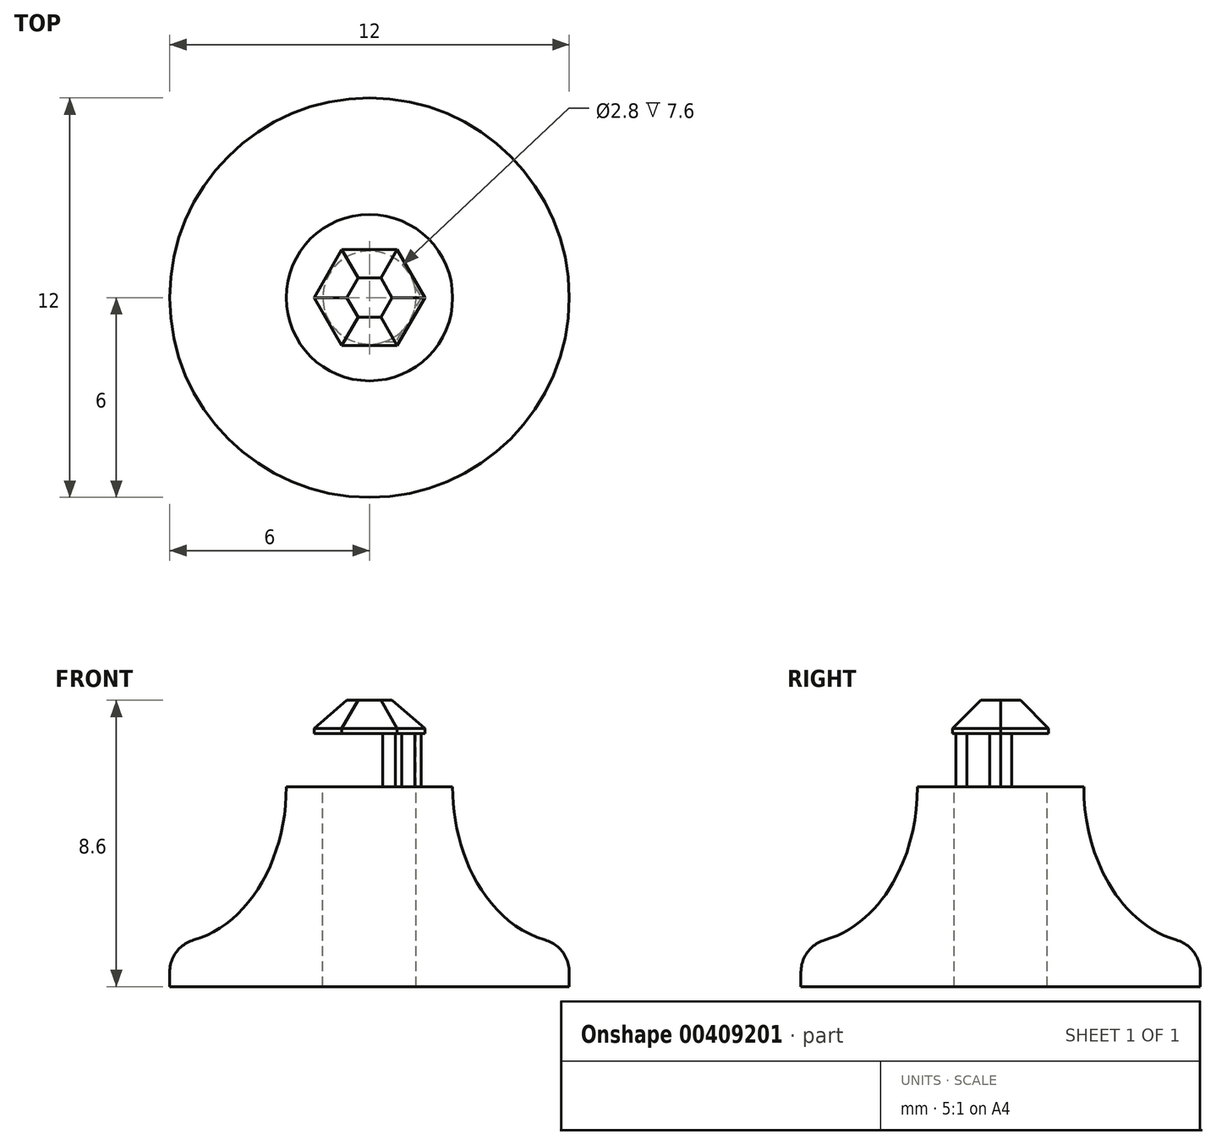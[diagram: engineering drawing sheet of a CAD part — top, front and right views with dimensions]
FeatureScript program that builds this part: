
annotation { "Feature Type Name" : "Feature", "Feature Type Description" : "" }
export const myFeature = defineFeature(function(context is Context, id is Id, definition is map)
    precondition{}
    {
        {
            var Q0;
            Q0=qCreatedBy(makeId("Front.planeOp"),FACE);
            var sketch = newSketch(context, id + "F0", { "sketchPlane" : qUnion([Q0])});
            skLineSegment(sketch, "E0.bottom", {"start": v(0, 0) * mm, "end": v(6, 0) * mm});
            skLineSegment(sketch, "E0.top", {"start": v(0, 6) * mm, "end": v(2.5, 6) * mm});
            skLineSegment(sketch, "E0.left", {"start": v(0, 0) * mm, "end": v(0, 6) * mm});
            skLineSegment(sketch, "E0.right", {"start": v(6, 0) * mm, "end": v(6, 0.44) * mm});
            skEllipticalArc(sketch, "E1", {});
            skPoint(sketch, "E2", {"position": v(2.5, 6) * mm});
            skPoint(sketch, "E3", {"position": v(6, 1.3) * mm});
            skPoint(sketch, "E4.visualSharp", {"position": v(0, 6) * mm});
            skArc(sketch, "E5.filletArc", {"start": v(6, 0.44) * mm, "mid": v(5.8, 1.04) * mm, "end": v(5.27, 1.4) * mm});
            const initialGuessF0  = {"E1": [0.006, 0.006, -1, 0, 0.0035, 0.0047, 6.283185307179586, 1.3618196011728392]};
            skSetInitialGuess(sketch, initialGuessF0);
            skSolve(sketch);
        }
        {
            var Q0;
            Q0=makeQuery(id+"F0.imprint","IMPRINT",FACE,{"disambiguationData":[TD([[makeQuery(id+"F0.imprint","IMPRINT",EDGE,{"derivedFrom":sQuery(id+"F0.wireOp",EDGE,"E0.bottom")}),1.0]])]});
            var Q1;
            Q1=sQuery(id+"F0.wireOp",EDGE,"E0.left");
            revolve(context, id + "F1", {"entities" : qUnion([Q0]), "axis" : qUnion([Q1]), "revolveType" : RevolveType.FULL});
        }
        {
            var Q0;
            Q0=makeQuery(id+"F1.opRevolve","SWEPT_BODY",BODY,{"disambiguationData":[OSD([sQuery(id+"F0.wireOp",EDGE,"E0.bottom"),sQuery(id+"F0.wireOp",EDGE,"E0.top"),sQuery(id+"F0.wireOp",EDGE,"E0.left"),sQuery(id+"F0.wireOp",EDGE,"E0.right"),sQuery(id+"F0.wireOp",EDGE,"E1"),sQuery(id+"F0.wireOp",EDGE,"ArTpo5st-Iq33-hNdW-1lph-2rlKh8i0XKDo"),sQuery(id+"F0.wireOp",EDGE,"E5.filletArc")])]});
            transform(context, id + "F2", {"entities" : qUnion([Q0]), "transformType" : TransformType.TRANSLATION_3D, "dx" : 0 * mm, "dy" : 0 * mm, "dz" : 0 * mm, "makeCopy" : true});
        }
        {
            var Q0;
            Q0=makeQuery(id+"F1.opRevolve","SWEPT_FACE",FACE,{"disambiguationData":[OSD([sQuery(id+"F0.wireOp",EDGE,"E0.top")])]});
            var sketch = newSketch(context, id + "F3", { "sketchPlane" : qUnion([Q0])});
            skCircle(sketch, "E6", {"center": v(0, 0) * mm, "radius": 1.4 * mm});
            skSolve(sketch);
        }
        {
            var Q0;
            Q0=makeQuery(id+"F3.imprint","IMPRINT",FACE,{"disambiguationData":[TD([[makeQuery(id+"F3.imprint","IMPRINT",EDGE,{"derivedFrom":sQuery(id+"F3.wireOp",EDGE,"E6")}),1.0]])]});
            extrude(context, id + "F4", {"entities" : qUnion([Q0]), "operationType" : NewBodyOperationType.REMOVE, "endBound" : BoundingType.THROUGH_ALL, "oppositeDirection" : true, "depth" : 25 * mm});
        }
        {
            var Q0;
            Q0=makeQuery(id+"F2.opPattern","COPY",FACE,{"derivedFrom":makeQuery(id+"F1.opRevolve","SWEPT_FACE",FACE,{"disambiguationData":[OSD([sQuery(id+"F0.wireOp",EDGE,"E0.top")])]}),"instanceName":"1"});
            var sketch = newSketch(context, id + "F5", { "sketchPlane" : qUnion([Q0])});
            skCircle(sketch, "E7.cCircle", {"center": v(0, 0) * mm, "radius": 1.34 * mm, "construction": true});
            skLineSegment(sketch, "E7.0", {"start": v(1.55, 0) * mm, "end": v(0.77, -1.34) * mm});
            skLineSegment(sketch, "E7.1", {"start": v(0.77, -1.34) * mm, "end": v(-0.78, -1.34) * mm});
            skLineSegment(sketch, "E7.2", {"start": v(-0.78, -1.34) * mm, "end": v(-1.55, 0) * mm});
            skLineSegment(sketch, "E7.3", {"start": v(-1.55, 0) * mm, "end": v(-0.77, 1.34) * mm});
            skLineSegment(sketch, "E7.4", {"start": v(-0.77, 1.34) * mm, "end": v(0.78, 1.34) * mm});
            skLineSegment(sketch, "E7.5", {"start": v(0.78, 1.34) * mm, "end": v(1.55, 0) * mm});
            skPoint(sketch, "E7.0.midPoint", {"position": v(1.16, -0.67) * mm});
            skSolve(sketch);
        }
        {
            var Q0;
            Q0=makeQuery(id+"F5.imprint","IMPRINT",FACE,{"disambiguationData":[TD([[makeQuery(id+"F5.imprint","IMPRINT",EDGE,{"derivedFrom":sQuery(id+"F5.wireOp",EDGE,"E7.0")}),-1.0]])]});
            extrude(context, id + "F6", {"entities" : qUnion([Q0]), "operationType" : NewBodyOperationType.ADD, "depth" : 1.6 * mm});
        }
        {
            var Q0;
            Q0=makeQuery(id+"F6.opExtrude","CAP_FACE",FACE,{"disambiguationData":[OSD([sQuery(id+"F5.wireOp",EDGE,"E7.0"),sQuery(id+"F5.wireOp",EDGE,"E7.1"),sQuery(id+"F5.wireOp",EDGE,"E7.2"),sQuery(id+"F5.wireOp",EDGE,"E7.3"),sQuery(id+"F5.wireOp",EDGE,"E7.4"),sQuery(id+"F5.wireOp",EDGE,"E7.5")])],"isStart":false});
            var sketch = newSketch(context, id + "F7", { "sketchPlane" : qUnion([Q0])});
            skLineSegment(sketch, "E8.0", {"start": v(-1.67, 0) * mm, "end": v(-0.83, 1.44) * mm});
            skLineSegment(sketch, "E8.1", {"start": v(0.83, 1.44) * mm, "end": v(1.67, 0) * mm});
            skLineSegment(sketch, "E8.2", {"start": v(1.67, 0) * mm, "end": v(0.83, -1.44) * mm});
            skLineSegment(sketch, "E8.3", {"start": v(-0.83, 1.44) * mm, "end": v(0.83, 1.44) * mm});
            skLineSegment(sketch, "E8.4", {"start": v(0.83, -1.44) * mm, "end": v(-0.83, -1.44) * mm});
            skLineSegment(sketch, "E8.5", {"start": v(-0.83, -1.44) * mm, "end": v(-1.67, 0) * mm});
            skSolve(sketch);
        }
        {
            var Q0;
            Q0 = qSketchRegion(id + "F7", true);
            extrude(context, id + "F8", {"entities" : qUnion([Q0]), "operationType" : NewBodyOperationType.ADD, "depth" : 1 * mm});
        }
        {
            var Q0;
            Q0=makeQuery(id+"F8.opExtrude","CAP_EDGE",EDGE,{"disambiguationData":[OSD([sQuery(id+"F7.wireOp",EDGE,"E8.5")])],"isStart":false});
            var Q1;
            Q1=makeQuery(id+"F8.opExtrude","CAP_EDGE",EDGE,{"disambiguationData":[OSD([sQuery(id+"F7.wireOp",EDGE,"E8.4")])],"isStart":false});
            var Q2;
            Q2=makeQuery(id+"F8.opExtrude","CAP_EDGE",EDGE,{"disambiguationData":[OSD([sQuery(id+"F7.wireOp",EDGE,"E8.0")])],"isStart":false});
            var Q3;
            Q3=makeQuery(id+"F8.opExtrude","CAP_EDGE",EDGE,{"disambiguationData":[OSD([sQuery(id+"F7.wireOp",EDGE,"E8.3")])],"isStart":false});
            var Q4;
            Q4=makeQuery(id+"F8.opExtrude","CAP_EDGE",EDGE,{"disambiguationData":[OSD([sQuery(id+"F7.wireOp",EDGE,"E8.1")])],"isStart":false});
            var Q5;
            Q5=makeQuery(id+"F8.opExtrude","CAP_EDGE",EDGE,{"disambiguationData":[OSD([sQuery(id+"F7.wireOp",EDGE,"E8.2")])],"isStart":false});
            chamfer(context, id + "F9", {"entities" : qUnion([Q0, Q1, Q2, Q3, Q4, Q5]), "width" : 0.85 * mm});
        }
    });
